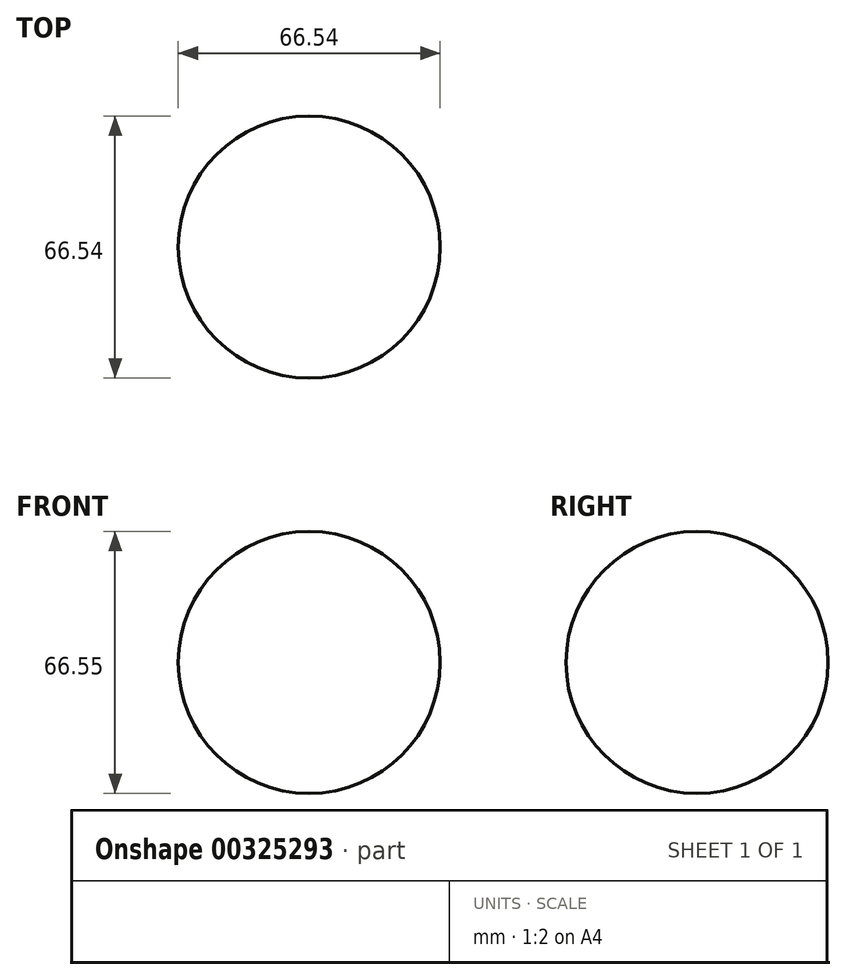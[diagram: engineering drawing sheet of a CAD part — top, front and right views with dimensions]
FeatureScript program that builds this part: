
annotation { "Feature Type Name" : "Feature", "Feature Type Description" : "" }
export const myFeature = defineFeature(function(context is Context, id is Id, definition is map)
    precondition{}
    {
        {
            var Q0;
            Q0=qCreatedBy(makeId("Front.planeOp"),FACE);
            var sketch = newSketch(context, id + "F0", { "sketchPlane" : qUnion([Q0])});
            skLineSegment(sketch, "E0", {"start": v(0, 0) * mm, "end": v(0, 63.02) * mm});
            skLineSegment(sketch, "E1", {"start": v(0, 0) * mm, "end": v(0, -63.02) * mm});
            skLineSegment(sketch, "E2", {"start": v(0, 63.02) * mm, "end": v(0, 29.74) * mm});
            skLineSegment(sketch, "E3", {"start": v(0, -63.02) * mm, "end": v(0, -38.79) * mm});
            skLineSegment(sketch, "E4", {"start": v(-13.08, -38.79) * mm, "end": v(-13.08, -63.02) * mm});
            skLineSegment(sketch, "E5", {"start": v(-13.08, -63.02) * mm, "end": v(0, -63.02) * mm});
            skArc(sketch, "E6", {"start": v(0, 63.02) * mm, "mid": v(-33.27, 29.74) * mm, "end": v(0, -3.53) * mm});
            skLineSegment(sketch, "E7", {"start": v(-17.35, -21.6) * mm, "end": v(-17.35, -33.8) * mm});
            skFitSpline(sketch, "E8", {"points": [v(-17.35, -33.8) * mm, v(-13.08, -38.79) * mm], "startDerivative": vector(1.64, -8.25) * mm, "endDerivative": vector(3.66, -5.66) * mm});
            skFitSpline(sketch, "E9", {"points": [v(-17.35, -21.6) * mm, v(-28.1, 11.91) * mm], "startDerivative": vector(-3.05, 39.7) * mm, "endDerivative": vector(-17.75, 35.74) * mm});
            skSolve(sketch);
        }
        {
            var Q0;
            {var subQ5=sQuery(id+"F0.wireOp",EDGE,"E0");Q0=makeQuery(id+"F0.imprint","IMPRINT",FACE,{"disambiguationData":[TD([[makeQuery(id+"F0.imprint","IMPRINT",EDGE,{"derivedFrom":subQ5}),1.0]])]});}
            var Q1;
            {var subQ3=sQuery(id+"F0.wireOp",EDGE,"q6tXODdP-kueP-3qUS-XKlc-TVd8Ke03fNmU");Q1=makeQuery(id+"F0.imprint","IMPRINT",FACE,{"disambiguationData":[TD([[makeQuery(id+"F0.imprint","IMPRINT",EDGE,{"derivedFrom":subQ3}),-1.0]])]});}
            var Q2;
            {var subQ1=sQuery(id+"F0.wireOp",EDGE,"XqtuEOKU-yWUW-HVgn-ajdv-bZRAP9Y5EIAn");Q2=makeQuery(id+"F0.imprint","IMPRINT",FACE,{"disambiguationData":[TD([[makeQuery(id+"F0.imprint","IMPRINT",EDGE,{"derivedFrom":subQ1}),-1.0]])]});}
            var Q3;
            Q3=makeQuery(id+"F0.imprint","IMPRINT",FACE,{"disambiguationData":[TD([[makeQuery(id+"F0.imprint","IMPRINT",EDGE,{"derivedFrom":sQuery(id+"F0.wireOp",EDGE,"E3")}),1.0]])]});
            var Q4;
            Q4=sQuery(id+"F0.wireOp",EDGE,"E0");
            revolve(context, id + "F1", {"entities" : qUnion([Q0, Q1, Q2, Q3]), "axis" : qUnion([Q4]), "revolveType" : RevolveType.FULL});
        }
    });
